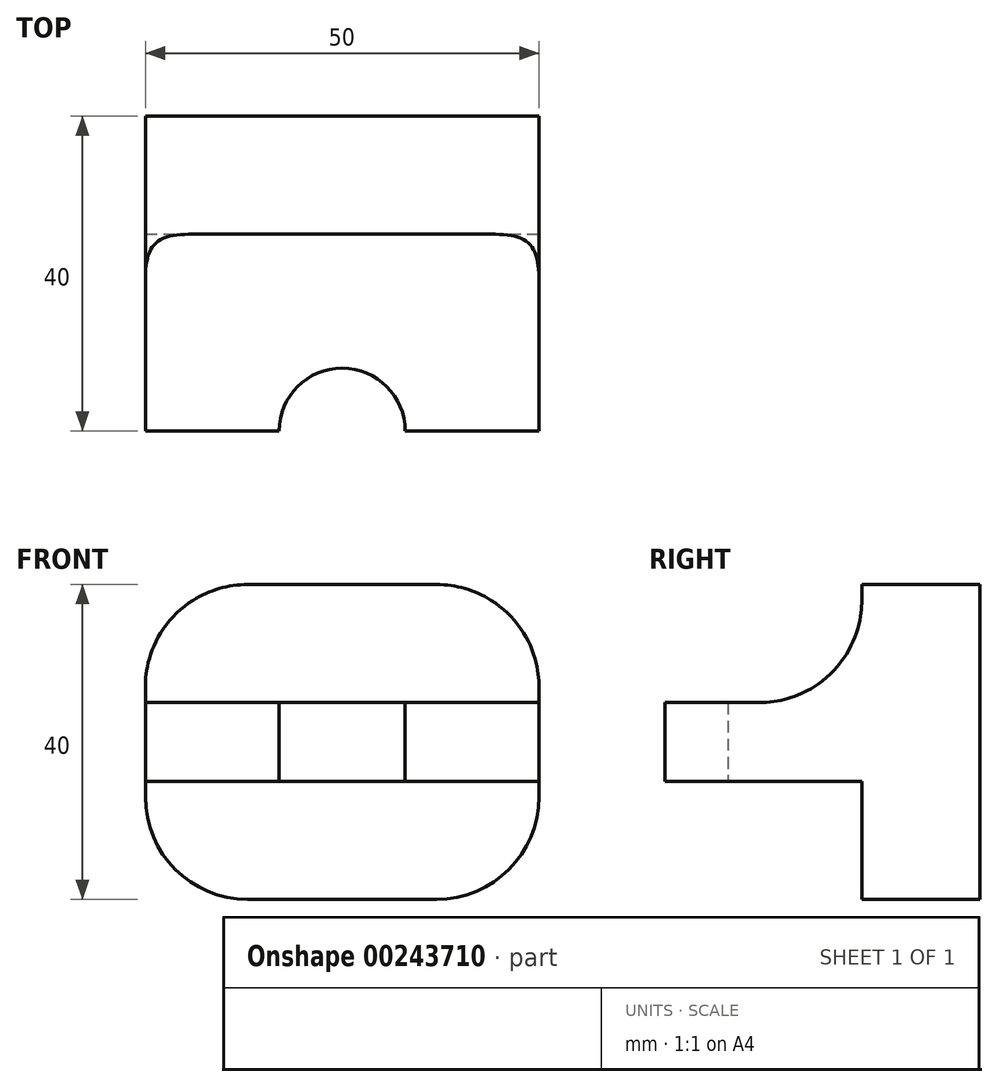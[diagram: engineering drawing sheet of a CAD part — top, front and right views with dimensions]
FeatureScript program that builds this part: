
annotation { "Feature Type Name" : "Feature", "Feature Type Description" : "" }
export const myFeature = defineFeature(function(context is Context, id is Id, definition is map)
    precondition{}
    {
        {
            var Q0;
            Q0=qCreatedBy(makeId("Front.planeOp"),FACE);
            var sketch = newSketch(context, id + "F0", { "sketchPlane" : qUnion([Q0])});
            skLineSegment(sketch, "E0.bottom", {"start": v(12, 20) * mm, "end": v(-12, 20) * mm});
            skLineSegment(sketch, "E0.top", {"start": v(12, -20) * mm, "end": v(-12, -20) * mm});
            skLineSegment(sketch, "E0.left", {"start": v(25, 7) * mm, "end": v(25, -7) * mm});
            skLineSegment(sketch, "E0.right", {"start": v(-25, 7) * mm, "end": v(-25, -7) * mm});
            skPoint(sketch, "E0.middle", {"position": v(0, 0) * mm});
            skPoint(sketch, "E1.visualSharp", {"position": v(-25, 20) * mm});
            skArc(sketch, "E1.filletArc", {"start": v(-12, 20) * mm, "mid": v(-21.2, 16.2) * mm, "end": v(-25, 7) * mm});
            skPoint(sketch, "E2.visualSharp", {"position": v(25, 20) * mm});
            skArc(sketch, "E2.filletArc", {"start": v(25, 7) * mm, "mid": v(21.2, 16.2) * mm, "end": v(12, 20) * mm});
            skPoint(sketch, "E3.visualSharp", {"position": v(25, -20) * mm});
            skArc(sketch, "E3.filletArc", {"start": v(12, -20) * mm, "mid": v(21.2, -16.2) * mm, "end": v(25, -7) * mm});
            skPoint(sketch, "E4.visualSharp", {"position": v(-25, -20) * mm});
            skArc(sketch, "E4.filletArc", {"start": v(-25, -7) * mm, "mid": v(-21.2, -16.2) * mm, "end": v(-12, -20) * mm});
            skSolve(sketch);
        }
        {
            var Q0;
            Q0=makeQuery(id+"F0.imprint","IMPRINT",FACE,{"disambiguationData":[TD([[makeQuery(id+"F0.imprint","IMPRINT",EDGE,{"derivedFrom":sQuery(id+"F0.wireOp",EDGE,"E0.bottom")}),1.0]])]});
            extrude(context, id + "F1", {"entities" : qUnion([Q0]), "oppositeDirection" : true, "depth" : 15 * mm});
        }
        {
            var Q0;
            Q0=qCreatedBy(makeId("Top.planeOp"),FACE);
            var sketch = newSketch(context, id + "F2", { "sketchPlane" : qUnion([Q0])});
            skLineSegment(sketch, "E5", {"start": v(-8, -25) * mm, "end": v(-25, -25) * mm});
            skLineSegment(sketch, "E6", {"start": v(-25, -25) * mm, "end": v(-25, 0) * mm});
            skLineSegment(sketch, "E7", {"start": v(-25, 0) * mm, "end": v(25, 0) * mm});
            skLineSegment(sketch, "E8", {"start": v(25, 0) * mm, "end": v(25, -25) * mm});
            skLineSegment(sketch, "E9", {"start": v(25, -25) * mm, "end": v(8, -25) * mm});
            skArc(sketch, "E10", {"start": v(8, -25) * mm, "mid": v(0, -17) * mm, "end": v(-8, -25) * mm});
            skSolve(sketch);
        }
        {
            var Q0;
            Q0=makeQuery(id+"F2.imprint","IMPRINT",FACE,{"disambiguationData":[TD([[makeQuery(id+"F2.imprint","IMPRINT",EDGE,{"derivedFrom":sQuery(id+"F2.wireOp",EDGE,"E5")}),-1.0]])]});
            extrude(context, id + "F3", {"entities" : qUnion([Q0]), "operationType" : NewBodyOperationType.ADD, "endBound" : BoundingType.SYMMETRIC, "depth" : 10 * mm});
        }
        {
            var Q0;
            Q0=makeQuery(id+"F3.opExtrude","CAP_EDGE",EDGE,{"disambiguationData":[OSD([sQuery(id+"F2.wireOp",EDGE,"E7")])],"isStart":false});
            var Q1;
            Q1=makeQuery(id+"F3.opExtrude","CAP_EDGE",EDGE,{"disambiguationData":[OSD([sQuery(id+"F2.wireOp",EDGE,"E7")])],"isStart":true});
            fillet(context, id + "F4", {"entities" : qUnion([Q0, Q1]), "radius" : 13 * mm, "tangentPropagation" : true, "allowEdgeOverflow" : false});
        }
    });
